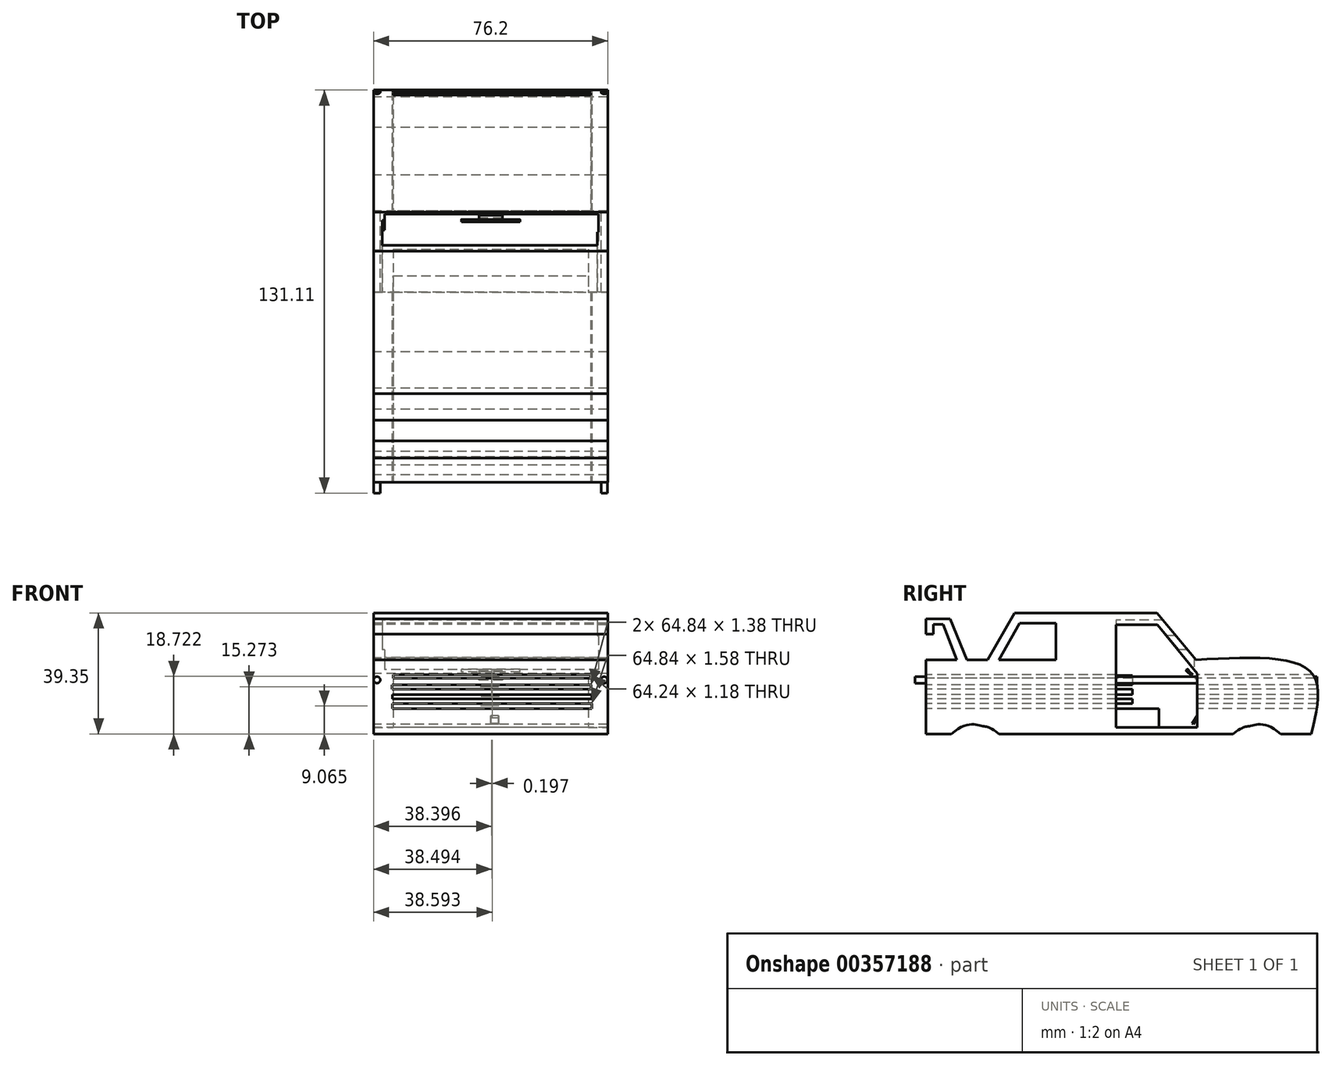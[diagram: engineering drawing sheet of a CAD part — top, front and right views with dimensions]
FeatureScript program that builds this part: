
annotation { "Feature Type Name" : "Feature", "Feature Type Description" : "" }
export const myFeature = defineFeature(function(context is Context, id is Id, definition is map)
    precondition{}
    {
        {
            var Q0;
            Q0=qCreatedBy(makeId("Right.planeOp"),FACE);
            var sketch = newSketch(context, id + "F0", { "sketchPlane" : qUnion([Q0])});
            skFitSpline(sketch, "E0", {"points": [v(63.5, 0) * mm, v(63.5, 20.01) * mm, v(26, 24.12) * mm], "startDerivative": vector(13.56, 55.42) * mm, "endDerivative": vector(-83.37, -4.53) * mm});
            skLineSegment(sketch, "E1", {"start": v(26, 24.12) * mm, "end": v(13.34, 39.35) * mm});
            skLineSegment(sketch, "E2", {"start": v(13.34, 39.35) * mm, "end": v(-33.06, 39.35) * mm});
            skLineSegment(sketch, "E3", {"start": v(-33.06, 39.35) * mm, "end": v(-41.73, 24.12) * mm});
            skLineSegment(sketch, "E4", {"start": v(-41.73, 24.12) * mm, "end": v(-61.89, 24.12) * mm});
            skLineSegment(sketch, "E5", {"start": v(-61.89, 24.12) * mm, "end": v(-61.89, 0) * mm});
            skLineSegment(sketch, "E6", {"start": v(-61.89, 0) * mm, "end": v(63.5, 0) * mm});
            skLineSegment(sketch, "E7", {"start": v(-48.48, 24.12) * mm, "end": v(-54, 37.44) * mm});
            skLineSegment(sketch, "E8", {"start": v(-51.81, 24.12) * mm, "end": v(-56.95, 37.44) * mm});
            skLineSegment(sketch, "E9", {"start": v(-56.95, 37.44) * mm, "end": v(-54, 37.44) * mm});
            skLineSegment(sketch, "E10.bottom", {"start": v(-56.95, 37.44) * mm, "end": v(-61.88, 37.44) * mm});
            skLineSegment(sketch, "E10.top", {"start": v(-59.42, 32.52) * mm, "end": v(-61.88, 32.52) * mm});
            skLineSegment(sketch, "E10.right", {"start": v(-61.88, 37.44) * mm, "end": v(-61.88, 32.52) * mm});
            skFitSpline(sketch, "E11", {"points": [v(-53.6, 0) * mm, v(-43.27, 2.52) * mm, v(-38.13, 0) * mm], "startDerivative": vector(26.5, 23.2) * mm, "endDerivative": vector(22.2, -17.87) * mm});
            skFitSpline(sketch, "E12.MirrorCS", {"points": [v(53.6, 0) * mm, v(43.27, 2.52) * mm, v(38.13, 0) * mm], "startDerivative": vector(-26.5, 23.2) * mm, "endDerivative": vector(-22.2, -17.87) * mm});
            skLineSegment(sketch, "E13", {"start": v(0, 35.47) * mm, "end": v(0, 19.7) * mm});
            skLineSegment(sketch, "E14", {"start": v(26.4, 19.7) * mm, "end": v(13.5, 35.47) * mm});
            skLineSegment(sketch, "E15", {"start": v(13.5, 35.47) * mm, "end": v(0, 35.47) * mm});
            skLineSegment(sketch, "E16", {"start": v(0, 19.7) * mm, "end": v(0, 2.11) * mm});
            skLineSegment(sketch, "E17", {"start": v(26.4, 2.11) * mm, "end": v(26.4, 19.7) * mm});
            skLineSegment(sketch, "E18", {"start": v(0, 2.11) * mm, "end": v(26.4, 2.11) * mm});
            skPoint(sketch, "E19.orphan", {"position": v(26.4, 0) * mm});
            skLineSegment(sketch, "E20", {"start": v(-59.42, 32.52) * mm, "end": v(-59.42, 35.7) * mm});
            skLineSegment(sketch, "E21", {"start": v(-59.42, 35.7) * mm, "end": v(-56.28, 35.7) * mm});
            skLineSegment(sketch, "E22", {"start": v(-32.52, 24.12) * mm, "end": v(-19.5, 24.12) * mm});
            skLineSegment(sketch, "E23", {"start": v(-19.5, 24.12) * mm, "end": v(-19.5, 36.06) * mm});
            skLineSegment(sketch, "E24", {"start": v(-19.5, 36.06) * mm, "end": v(-31.33, 36.06) * mm});
            skLineSegment(sketch, "E25", {"start": v(-31.33, 36.06) * mm, "end": v(-38.13, 24.12) * mm});
            skLineSegment(sketch, "E26", {"start": v(-38.13, 24.12) * mm, "end": v(-32.52, 24.12) * mm});
            skSolve(sketch);
        }
        {
            var Q0;
            Q0=makeQuery(id+"F0.imprint","IMPRINT",FACE,{"disambiguationData":[TD([[makeQuery(id+"F0.imprint","IMPRINT",EDGE,{"derivedFrom":sQuery(id+"F0.wireOp",EDGE,"E10.bottom")}),1.0]])]});
            var Q1;
            {var subQ0=sQuery(id+"F0.wireOp",EDGE,"E10.left");Q1=makeQuery(id+"F0.imprint","IMPRINT",FACE,{"disambiguationData":[TD([[makeQuery(id+"F0.imprint","IMPRINT",EDGE,{"derivedFrom":subQ0}),1.0]])]});}
            var Q2;
            {var subQ4=sQuery(id+"F0.wireOp",EDGE,"E7");Q2=makeQuery(id+"F0.imprint","IMPRINT",FACE,{"disambiguationData":[TD([[makeQuery(id+"F0.imprint","IMPRINT",EDGE,{"derivedFrom":subQ4}),1.0]])]});}
            var Q3;
            {var subQ9=sQuery(id+"F0.wireOp",EDGE,"E0");Q3=makeQuery(id+"F0.imprint","IMPRINT",FACE,{"disambiguationData":[TD([[makeQuery(id+"F0.imprint","IMPRINT",EDGE,{"derivedFrom":subQ9}),1.0]])]});}
            extrude(context, id + "F1", {"entities" : qUnion([Q0, Q1, Q2, Q3]), "endBound" : BoundingType.SYMMETRIC, "depth" : 76.2 * mm});
        }
        {
            var Q0;
            Q0=qCreatedBy(makeId("Right.planeOp"),FACE);
            var sketch = newSketch(context, id + "F2", { "sketchPlane" : qUnion([Q0])});
            skLineSegment(sketch, "E27", {"start": v(0, 28.77) * mm, "end": v(5.32, 28.77) * mm});
            skLineSegment(sketch, "E28", {"start": v(5.32, 28.77) * mm, "end": v(5.32, 9.85) * mm});
            skLineSegment(sketch, "E29", {"start": v(5.32, 9.85) * mm, "end": v(14, 9.85) * mm});
            skLineSegment(sketch, "E30", {"start": v(14, 9.85) * mm, "end": v(14, 2.1) * mm});
            skLineSegment(sketch, "E31", {"start": v(0, 28.77) * mm, "end": v(0, 2.1) * mm});
            skLineSegment(sketch, "E32", {"start": v(0, 2.1) * mm, "end": v(14, 2.1) * mm});
            skLineSegment(sketch, "E33", {"start": v(26.4, 5.91) * mm, "end": v(24.75, 3.33) * mm});
            skLineSegment(sketch, "E34", {"start": v(24.75, 3.33) * mm, "end": v(25.12, 3.1) * mm});
            skLineSegment(sketch, "E35", {"start": v(25.12, 3.1) * mm, "end": v(26.4, 5.1) * mm});
            skLineSegment(sketch, "E36", {"start": v(26.4, 5.1) * mm, "end": v(26.4, 5.91) * mm});
            skSolve(sketch);
        }
        {
            var Q0;
            Q0=makeQuery(id+"F2.imprint","IMPRINT",FACE,{"disambiguationData":[TD([[makeQuery(id+"F2.imprint","IMPRINT",EDGE,{"derivedFrom":sQuery(id+"F2.wireOp",EDGE,"E27")}),-1.0]])]});
            extrude(context, id + "F3", {"entities" : qUnion([Q0]), "operationType" : NewBodyOperationType.ADD, "endBound" : BoundingType.SYMMETRIC, "depth" : 63.5 * mm});
        }
        {
            var Q0;
            Q0=makeQuery(id+"F2.imprint","IMPRINT",FACE,{"disambiguationData":[TD([[makeQuery(id+"F2.imprint","IMPRINT",EDGE,{"derivedFrom":sQuery(id+"F2.wireOp",EDGE,"E33")}),1.0]])]});
            extrude(context, id + "F4", {"entities" : qUnion([Q0]), "depth" : 2.54 * mm});
        }
        {
            var Q0;
            Q0=qCreatedBy(makeId("Front.planeOp"),FACE);
            var sketch = newSketch(context, id + "F5", { "sketchPlane" : qUnion([Q0])});
            skLineSegment(sketch, "E37.bottom", {"start": v(34.68, 37.05) * mm, "end": v(-35.28, 37.05) * mm});
            skLineSegment(sketch, "E37.top", {"start": v(34.68, 27.4) * mm, "end": v(-35.28, 27.4) * mm});
            skLineSegment(sketch, "E37.left", {"start": v(34.68, 37.05) * mm, "end": v(34.68, 27.4) * mm});
            skLineSegment(sketch, "E37.right", {"start": v(-35.28, 37.05) * mm, "end": v(-35.28, 27.4) * mm});
            skSolve(sketch);
        }
        {
            var Q0;
            Q0 = qSketchRegion(id + "F5", true);
            extrude(context, id + "F6", {"entities" : qUnion([Q0]), "operationType" : NewBodyOperationType.REMOVE, "oppositeDirection" : true, "depth" : 25.4 * mm});
        }
        {
            var Q0;
            Q0=qCreatedBy(makeId("Front.planeOp"),FACE);
            var sketch = newSketch(context, id + "F7", { "sketchPlane" : qUnion([Q0])});
            skLineSegment(sketch, "E38.bottom", {"start": v(-34.57, 31.9) * mm, "end": v(35.09, 31.9) * mm});
            skLineSegment(sketch, "E38.top", {"start": v(-34.57, 18.95) * mm, "end": v(35.09, 18.95) * mm});
            skLineSegment(sketch, "E38.left", {"start": v(-34.57, 31.9) * mm, "end": v(-34.57, 18.95) * mm});
            skLineSegment(sketch, "E38.right", {"start": v(35.09, 31.9) * mm, "end": v(35.09, 18.95) * mm});
            skSolve(sketch);
        }
        {
            var Q0;
            Q0 = qSketchRegion(id + "F7", true);
            extrude(context, id + "F8", {"entities" : qUnion([Q0]), "operationType" : NewBodyOperationType.REMOVE, "oppositeDirection" : true, "depth" : 25.4 * mm});
        }
        {
            var Q0;
            Q0=qCreatedBy(makeId("Right.planeOp"),FACE);
            var sketch = newSketch(context, id + "F9", { "sketchPlane" : qUnion([Q0])});
            skLineSegment(sketch, "E39", {"start": v(25.28, 19.07) * mm, "end": v(23.65, 20.6) * mm});
            skLineSegment(sketch, "E40", {"start": v(23.27, 20.2) * mm, "end": v(24.64, 18.92) * mm});
            skCircle(sketch, "E41", {"center": v(23.23, 20.6) * mm, "radius": 0.41 * mm});
            skLineSegment(sketch, "E42", {"start": v(25.28, 19.07) * mm, "end": v(26.43, 18.09) * mm});
            skLineSegment(sketch, "E43", {"start": v(26.43, 18.09) * mm, "end": v(26.43, 17.48) * mm});
            skLineSegment(sketch, "E44", {"start": v(26.43, 17.48) * mm, "end": v(24.64, 18.92) * mm});
            skSolve(sketch);
        }
        {
            var Q0;
            {var subQ0=sQuery(id+"F9.wireOp",EDGE,"E39");Q0=makeQuery(id+"F9.imprint","IMPRINT",FACE,{"disambiguationData":[TD([[makeQuery(id+"F9.imprint","IMPRINT",EDGE,{"derivedFrom":subQ0}),1.0]])]});}
            extrude(context, id + "F10", {"entities" : qUnion([Q0]), "endBound" : BoundingType.SYMMETRIC, "depth" : 7.62 * mm});
        }
        {
            var Q0;
            {var subQ0=sQuery(id+"F9.wireOp",EDGE,"E41");var subQ1=makeQuery(id+"F9.imprint","INTERSECT",VERTEX,{"derivedFrom":[sQuery(id+"F9.wireOp",EDGE,"E39"),subQ0]});Q0=makeQuery(id+"F9.imprint","IMPRINT",FACE,{"disambiguationData":[TD([[makeQuery(id+"F9.imprint","IMPRINT",EDGE,{"disambiguationData":[TD([[subQ1,1.0]])],"derivedFrom":subQ0}),1.0]])]});}
            extrude(context, id + "F11", {"entities" : qUnion([Q0]), "operationType" : NewBodyOperationType.ADD, "endBound" : BoundingType.SYMMETRIC, "depth" : 19.05 * mm});
        }
        {
            var Q0;
            Q0=qCreatedBy(makeId("Front.planeOp"),FACE);
            var sketch = newSketch(context, id + "F12", { "sketchPlane" : qUnion([Q0])});
            skCircle(sketch, "E45", {"center": v(36.97, 17.58) * mm, "radius": 1.06 * mm});
            skCircle(sketch, "E46.MirrorC", {"center": v(-36.97, 17.58) * mm, "radius": 1.06 * mm});
            skSolve(sketch);
        }
        {
            var Q0;
            Q0 = qSketchRegion(id + "F12", true);
            extrude(context, id + "F13", {"entities" : qUnion([Q0]), "operationType" : NewBodyOperationType.ADD, "endBound" : BoundingType.SYMMETRIC, "depth" : 130.8 * mm});
        }
        {
            var Q0;
            Q0=qCreatedBy(makeId("Front.planeOp"),FACE);
            var sketch = newSketch(context, id + "F14", { "sketchPlane" : qUnion([Q0])});
            skLineSegment(sketch, "E47.bottom", {"start": v(32.52, 19.31) * mm, "end": v(-31.73, 19.31) * mm});
            skLineSegment(sketch, "E47.top", {"start": v(32.52, 18.13) * mm, "end": v(-31.73, 18.13) * mm});
            skLineSegment(sketch, "E47.left", {"start": v(32.52, 19.31) * mm, "end": v(32.52, 18.13) * mm});
            skLineSegment(sketch, "E47.right", {"start": v(-31.73, 19.31) * mm, "end": v(-31.73, 18.13) * mm});
            skLineSegment(sketch, "E48.bottom", {"start": v(32.71, 15.96) * mm, "end": v(-32.12, 15.96) * mm});
            skLineSegment(sketch, "E48.top", {"start": v(32.71, 14.58) * mm, "end": v(-32.12, 14.58) * mm});
            skLineSegment(sketch, "E48.left", {"start": v(32.71, 15.96) * mm, "end": v(32.71, 14.58) * mm});
            skLineSegment(sketch, "E48.right", {"start": v(-32.12, 15.96) * mm, "end": v(-32.12, 14.58) * mm});
            skLineSegment(sketch, "E49.bottom", {"start": v(32.91, 11.43) * mm, "end": v(-31.93, 11.43) * mm});
            skLineSegment(sketch, "E49.top", {"start": v(32.91, 12.8) * mm, "end": v(-31.93, 12.8) * mm});
            skLineSegment(sketch, "E49.left", {"start": v(32.91, 11.43) * mm, "end": v(32.91, 12.8) * mm});
            skLineSegment(sketch, "E49.right", {"start": v(-31.93, 11.43) * mm, "end": v(-31.93, 12.8) * mm});
            skLineSegment(sketch, "E50.bottom", {"start": v(32.91, 8.28) * mm, "end": v(-31.93, 8.28) * mm});
            skLineSegment(sketch, "E50.top", {"start": v(32.91, 9.85) * mm, "end": v(-31.93, 9.85) * mm});
            skLineSegment(sketch, "E50.left", {"start": v(32.91, 8.28) * mm, "end": v(32.91, 9.85) * mm});
            skLineSegment(sketch, "E50.right", {"start": v(-31.93, 8.28) * mm, "end": v(-31.93, 9.85) * mm});
            skSolve(sketch);
        }
        {
            var Q0;
            Q0 = qSketchRegion(id + "F14", true);
            extrude(context, id + "F15", {"entities" : qUnion([Q0]), "operationType" : NewBodyOperationType.REMOVE, "endBound" : BoundingType.SYMMETRIC, "oppositeDirection" : true, "depth" : 152.4 * mm});
        }
    });
